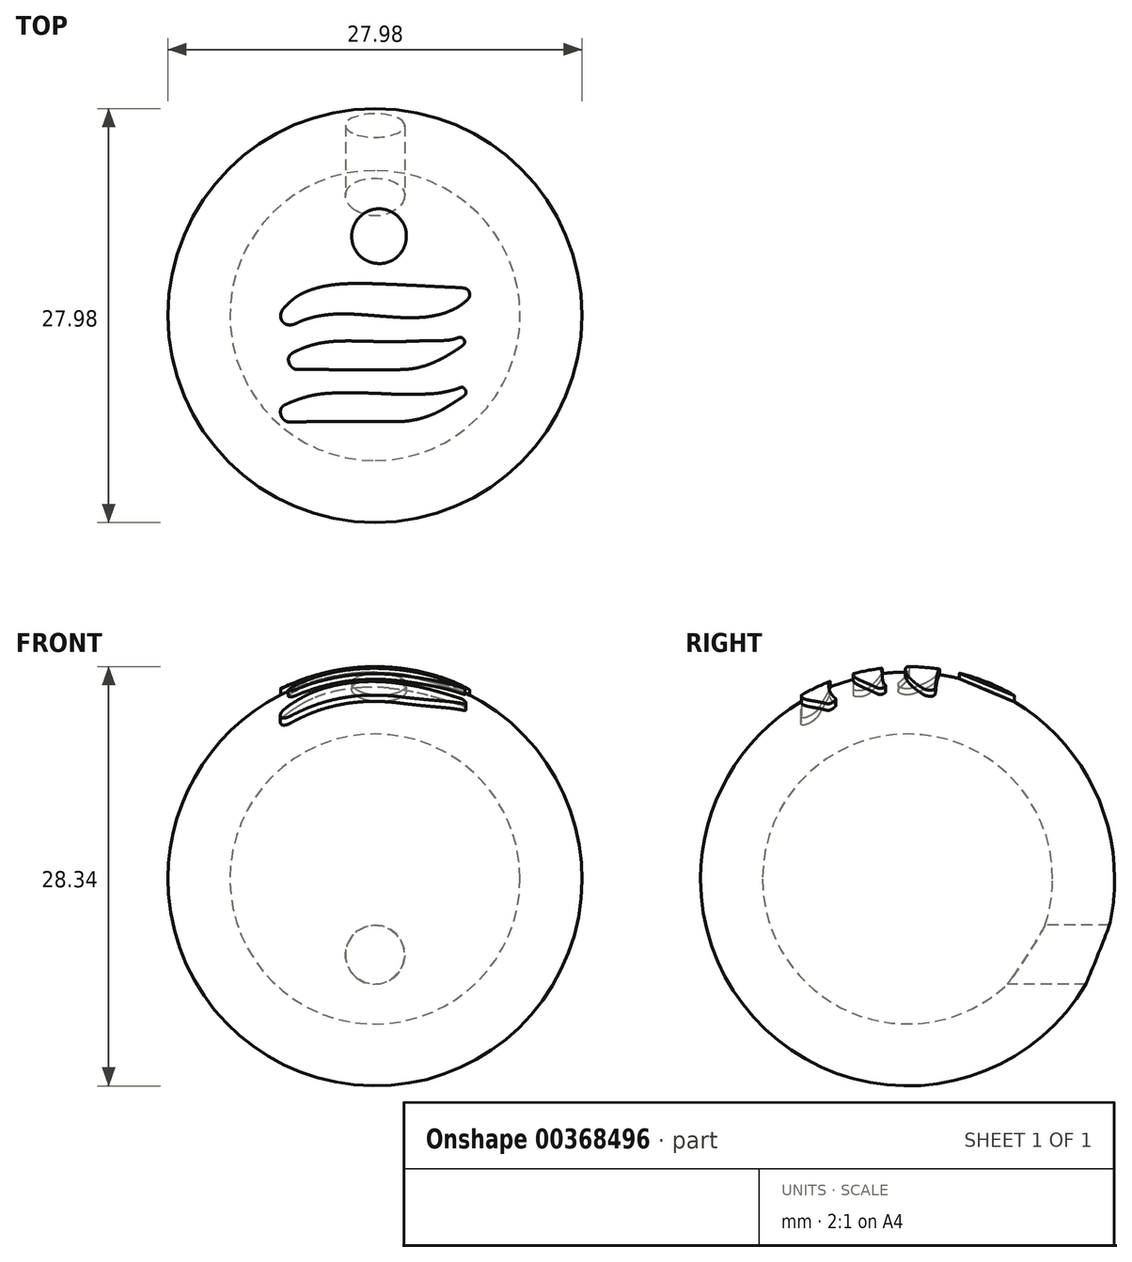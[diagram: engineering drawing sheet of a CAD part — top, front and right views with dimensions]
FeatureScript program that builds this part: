
annotation { "Feature Type Name" : "Feature", "Feature Type Description" : "" }
export const myFeature = defineFeature(function(context is Context, id is Id, definition is map)
    precondition{}
    {
        {
            var Q0;
            Q0=qCreatedBy(makeId("Top.planeOp"),FACE);
            var sketch = newSketch(context, id + "F0", { "sketchPlane" : qUnion([Q0])});
            skLineSegment(sketch, "E0", {"start": v(0, -10) * mm, "end": v(0, 10) * mm});
            skArc(sketch, "E1", {"start": v(0, 10) * mm, "mid": v(-10, 0) * mm, "end": v(0, -10) * mm});
            skSolve(sketch);
        }
        {
            var Q0;
            {var subQ0=sQuery(id+"F0.wireOp",EDGE,"E1");Q0=makeQuery(id+"F0.imprint","IMPRINT",FACE,{"disambiguationData":[TD([[makeQuery(id+"F0.imprint","IMPRINT",EDGE,{"derivedFrom":subQ0}),1.0]])]});}
            var Q1;
            Q1=sQuery(id+"F0.wireOp",EDGE,"E0");
            revolve(context, id + "F1", {"entities" : qUnion([Q0]), "axis" : qUnion([Q1]), "revolveType" : RevolveType.FULL});
        }
        {
            var Q0;
            Q0=makeQuery(id+"F1.opRevolve","SWEPT_BODY",BODY,{"disambiguationData":[OSD([sQuery(id+"F0.wireOp",EDGE,"E0"),sQuery(id+"F0.wireOp",EDGE,"E1")])]});
            var Q1;
            Q1=sQuery(id+"F0.wireOp",VERTEX,"NPe4G0ez-t7S9-9isL-QO5v-uuJu600mHcIT.center");
            var Q2;
            Q2=sQuery(id+"F0.wireOp",VERTEX,"E1.center");
            transform(context, id + "F2", {"entities" : qUnion([Q0]), "transformType" : TransformType.SCALE_UNIFORMLY, "scale" : 33.3, "scalePoint" : qUnion([Q2]), "makeCopy" : false});
        }
        {
            var Q0;
            Q0=qCreatedBy(makeId("Top.planeOp"),FACE);
            var sketch = newSketch(context, id + "F3", { "sketchPlane" : qUnion([Q0])});
            skArc(sketch, "E2", {"start": v(-4.66, 170.28) * mm, "mid": v(-7.58, 169.39) * mm, "end": v(-10.43, 168.3) * mm});
            skArc(sketch, "E3", {"start": v(-10.43, 168.3) * mm, "mid": v(-13.1, 167.06) * mm, "end": v(-15.68, 165.63) * mm});
            skArc(sketch, "E4", {"start": v(-15.68, 165.63) * mm, "mid": v(-18.2, 163.97) * mm, "end": v(-20.58, 162.14) * mm});
            skArc(sketch, "E5", {"start": v(-20.58, 162.14) * mm, "mid": v(-23, 160) * mm, "end": v(-25.3, 157.73) * mm});
            skArc(sketch, "E6", {"start": v(-25.3, 157.73) * mm, "mid": v(-31.47, 149.54) * mm, "end": v(-35.58, 140.15) * mm});
            skArc(sketch, "E7", {"start": v(-35.58, 140.15) * mm, "mid": v(-37.42, 130.07) * mm, "end": v(-36.87, 119.84) * mm});
            skArc(sketch, "E8", {"start": v(-36.87, 119.84) * mm, "mid": v(-33.98, 110.06) * mm, "end": v(-28.9, 101.23) * mm});
            skArc(sketch, "E9", {"start": v(-28.9, 101.23) * mm, "mid": v(-21.93, 93.88) * mm, "end": v(-13.42, 88.39) * mm});
            skArc(sketch, "E10", {"start": v(-13.42, 88.39) * mm, "mid": v(-4.52, 85.1) * mm, "end": v(4.86, 83.64) * mm});
            skArc(sketch, "E11", {"start": v(4.86, 83.64) * mm, "mid": v(14.1, 84.14) * mm, "end": v(23, 86.6) * mm});
            skArc(sketch, "E12", {"start": v(23, 86.6) * mm, "mid": v(31.14, 90.88) * mm, "end": v(38.15, 96.82) * mm});
            skArc(sketch, "E13", {"start": v(38.15, 96.82) * mm, "mid": v(43.87, 104.23) * mm, "end": v(47.95, 112.66) * mm});
            skArc(sketch, "E14", {"start": v(47.95, 112.66) * mm, "mid": v(48.9, 115.67) * mm, "end": v(49.58, 118.75) * mm});
            skArc(sketch, "E15", {"start": v(49.58, 118.75) * mm, "mid": v(50.08, 122.26) * mm, "end": v(50.36, 125.8) * mm});
            skArc(sketch, "E16", {"start": v(50.36, 125.8) * mm, "mid": v(50.43, 129.3) * mm, "end": v(50.27, 132.82) * mm});
            skArc(sketch, "E17", {"start": v(50.27, 132.82) * mm, "mid": v(49.9, 135.86) * mm, "end": v(49.24, 138.85) * mm});
            skArc(sketch, "E18", {"start": v(49.24, 138.85) * mm, "mid": v(46.19, 146.9) * mm, "end": v(41.61, 154.2) * mm});
            skArc(sketch, "E19", {"start": v(41.61, 154.2) * mm, "mid": v(35.64, 160.54) * mm, "end": v(28.58, 165.62) * mm});
            skArc(sketch, "E20", {"start": v(28.58, 165.62) * mm, "mid": v(20.7, 169.25) * mm, "end": v(12.28, 171.3) * mm});
            skArc(sketch, "E21", {"start": v(12.28, 171.3) * mm, "mid": v(3.76, 171.65) * mm, "end": v(-4.66, 170.28) * mm});
            skArc(sketch, "E22", {"start": v(-53.26, 50.77) * mm, "mid": v(-64.06, 49.8) * mm, "end": v(-74.8, 48.33) * mm});
            skArc(sketch, "E23", {"start": v(-74.8, 48.33) * mm, "mid": v(-84.6, 46.48) * mm, "end": v(-94.27, 44.06) * mm});
            skArc(sketch, "E24", {"start": v(-94.27, 44.06) * mm, "mid": v(-102.95, 41.3) * mm, "end": v(-111.44, 38.01) * mm});
            skArc(sketch, "E25", {"start": v(-111.44, 38.01) * mm, "mid": v(-118.91, 34.44) * mm, "end": v(-126.06, 30.25) * mm});
            skArc(sketch, "E26", {"start": v(-126.06, 30.25) * mm, "mid": v(-129.48, 27.88) * mm, "end": v(-132.74, 25.3) * mm});
            skArc(sketch, "E27", {"start": v(-132.74, 25.3) * mm, "mid": v(-136.56, 21.93) * mm, "end": v(-140.26, 18.43) * mm});
            skArc(sketch, "E28", {"start": v(-140.26, 18.43) * mm, "mid": v(-143.63, 15) * mm, "end": v(-146.88, 11.47) * mm});
            skArc(sketch, "E29", {"start": v(-146.88, 11.47) * mm, "mid": v(-148.63, 9.2) * mm, "end": v(-150.04, 6.7) * mm});
            skArc(sketch, "E30", {"start": v(-150.04, 6.7) * mm, "mid": v(-151.12, 3.79) * mm, "end": v(-151.7, 0.72) * mm});
            skArc(sketch, "E31", {"start": v(-151.7, 0.72) * mm, "mid": v(-151.7, -2.28) * mm, "end": v(-151.14, -5.22) * mm});
            skArc(sketch, "E32", {"start": v(-151.14, -5.22) * mm, "mid": v(-150.05, -7.88) * mm, "end": v(-148.44, -10.26) * mm});
            skArc(sketch, "E33", {"start": v(-148.44, -10.26) * mm, "mid": v(-146.42, -12.22) * mm, "end": v(-144.02, -13.69) * mm});
            skArc(sketch, "E34", {"start": v(-144.02, -13.69) * mm, "mid": v(-142.01, -14.5) * mm, "end": v(-139.92, -15.03) * mm});
            skArc(sketch, "E35", {"start": v(-139.92, -15.03) * mm, "mid": v(-137.8, -15.3) * mm, "end": v(-135.66, -15.27) * mm});
            skArc(sketch, "E36", {"start": v(-135.66, -15.27) * mm, "mid": v(-133.36, -14.96) * mm, "end": v(-131.12, -14.38) * mm});
            skArc(sketch, "E37", {"start": v(-131.12, -14.38) * mm, "mid": v(-128.6, -13.46) * mm, "end": v(-126.17, -12.35) * mm});
            skArc(sketch, "E38", {"start": v(-126.17, -12.35) * mm, "mid": v(-117.46, -8.41) * mm, "end": v(-108.44, -5.24) * mm});
            skArc(sketch, "E39", {"start": v(-108.44, -5.24) * mm, "mid": v(-98.18, -2.46) * mm, "end": v(-87.78, -0.33) * mm});
            skArc(sketch, "E40", {"start": v(-87.78, -0.33) * mm, "mid": v(-76.35, 1.3) * mm, "end": v(-64.84, 2.26) * mm});
            skArc(sketch, "E41", {"start": v(-64.84, 2.26) * mm, "mid": v(-52.55, 2.64) * mm, "end": v(-40.26, 2.43) * mm});
            skArc(sketch, "E42", {"start": v(-40.26, 2.43) * mm, "mid": v(-36.4, 2.26) * mm, "end": v(-32.52, 2.05) * mm});
            skArc(sketch, "E43", {"start": v(-32.52, 2.05) * mm, "mid": v(-27.36, 1.73) * mm, "end": v(-22.2, 1.4) * mm});
            skArc(sketch, "E44", {"start": v(-22.2, 1.4) * mm, "mid": v(-16.72, 1.02) * mm, "end": v(-11.24, 0.63) * mm});
            skArc(sketch, "E45", {"start": v(-11.24, 0.63) * mm, "mid": v(-6.25, 0.24) * mm, "end": v(-1.26, -0.16) * mm});
            skArc(sketch, "E46", {"start": v(-1.26, -0.16) * mm, "mid": v(3.81, -0.58) * mm, "end": v(8.89, -0.98) * mm});
            skArc(sketch, "E47", {"start": v(8.89, -0.98) * mm, "mid": v(14.64, -1.41) * mm, "end": v(20.4, -1.83) * mm});
            skArc(sketch, "E48", {"start": v(20.4, -1.83) * mm, "mid": v(25.93, -2.22) * mm, "end": v(31.47, -2.59) * mm});
            skArc(sketch, "E49", {"start": v(31.47, -2.59) * mm, "mid": v(35.82, -2.86) * mm, "end": v(40.17, -3.11) * mm});
            skArc(sketch, "E50", {"start": v(40.17, -3.11) * mm, "mid": v(56.95, -3.55) * mm, "end": v(73.73, -3.04) * mm});
            skArc(sketch, "E51", {"start": v(73.73, -3.04) * mm, "mid": v(87.98, -1.56) * mm, "end": v(102.05, 1.2) * mm});
            skArc(sketch, "E52", {"start": v(102.05, 1.2) * mm, "mid": v(114.17, 4.83) * mm, "end": v(125.84, 9.71) * mm});
            skArc(sketch, "E53", {"start": v(125.84, 9.71) * mm, "mid": v(136.2, 15.52) * mm, "end": v(145.73, 22.6) * mm});
            skArc(sketch, "E54", {"start": v(145.73, 22.6) * mm, "mid": v(146.55, 23.31) * mm, "end": v(147.35, 24.05) * mm});
            skArc(sketch, "E55", {"start": v(147.35, 24.05) * mm, "mid": v(148.14, 24.82) * mm, "end": v(148.9, 25.62) * mm});
            skArc(sketch, "E56", {"start": v(148.9, 25.62) * mm, "mid": v(149.57, 26.35) * mm, "end": v(150.21, 27.1) * mm});
            skArc(sketch, "E57", {"start": v(150.21, 27.1) * mm, "mid": v(150.6, 27.61) * mm, "end": v(150.94, 28.16) * mm});
            skArc(sketch, "E58", {"start": v(150.94, 28.16) * mm, "mid": v(151.52, 29.44) * mm, "end": v(151.89, 30.8) * mm});
            skArc(sketch, "E59", {"start": v(151.89, 30.8) * mm, "mid": v(152.1, 32.43) * mm, "end": v(152.15, 34.07) * mm});
            skArc(sketch, "E60", {"start": v(152.15, 34.07) * mm, "mid": v(152.02, 35.68) * mm, "end": v(151.74, 37.26) * mm});
            skArc(sketch, "E61", {"start": v(151.74, 37.26) * mm, "mid": v(151.32, 38.5) * mm, "end": v(150.68, 39.64) * mm});
            skArc(sketch, "E62", {"start": v(150.68, 39.64) * mm, "mid": v(149.45, 41.07) * mm, "end": v(147.96, 42.23) * mm});
            skArc(sketch, "E63", {"start": v(147.96, 42.23) * mm, "mid": v(146.18, 43.15) * mm, "end": v(144.28, 43.77) * mm});
            skArc(sketch, "E64", {"start": v(144.28, 43.77) * mm, "mid": v(141.31, 44.35) * mm, "end": v(138.3, 44.68) * mm});
            skArc(sketch, "E65", {"start": v(138.3, 44.68) * mm, "mid": v(132.52, 45.03) * mm, "end": v(126.74, 45.3) * mm});
            skArc(sketch, "E66", {"start": v(126.74, 45.3) * mm, "mid": v(122.24, 45.48) * mm, "end": v(117.75, 45.68) * mm});
            skArc(sketch, "E67", {"start": v(117.75, 45.68) * mm, "mid": v(110.73, 46) * mm, "end": v(103.71, 46.34) * mm});
            skArc(sketch, "E68", {"start": v(103.71, 46.34) * mm, "mid": v(95.78, 46.73) * mm, "end": v(87.84, 47.12) * mm});
            skArc(sketch, "E69", {"start": v(87.84, 47.12) * mm, "mid": v(80.04, 47.51) * mm, "end": v(72.24, 47.91) * mm});
            skArc(sketch, "E70", {"start": v(72.24, 47.91) * mm, "mid": v(47.98, 49.13) * mm, "end": v(23.71, 50.25) * mm});
            skArc(sketch, "E71", {"start": v(23.71, 50.25) * mm, "mid": v(7.3, 50.9) * mm, "end": v(-9.1, 51.36) * mm});
            skArc(sketch, "E72", {"start": v(-9.1, 51.36) * mm, "mid": v(-21.25, 51.54) * mm, "end": v(-33.4, 51.52) * mm});
            skArc(sketch, "E73", {"start": v(-33.4, 51.52) * mm, "mid": v(-43.34, 51.29) * mm, "end": v(-53.26, 50.77) * mm});
            skArc(sketch, "E74", {"start": v(132.24, -36.27) * mm, "mid": v(128.84, -37.48) * mm, "end": v(125.36, -38.43) * mm});
            skArc(sketch, "E75", {"start": v(125.36, -38.43) * mm, "mid": v(121.58, -39.19) * mm, "end": v(117.76, -39.7) * mm});
            skArc(sketch, "E76", {"start": v(117.76, -39.7) * mm, "mid": v(112.5, -40.14) * mm, "end": v(107.22, -40.38) * mm});
            skArc(sketch, "E77", {"start": v(107.22, -40.38) * mm, "mid": v(98.48, -40.56) * mm, "end": v(89.74, -40.66) * mm});
            skArc(sketch, "E78", {"start": v(89.74, -40.66) * mm, "mid": v(84.02, -40.72) * mm, "end": v(78.3, -40.8) * mm});
            skArc(sketch, "E79", {"start": v(78.3, -40.8) * mm, "mid": v(72.28, -40.94) * mm, "end": v(66.26, -41.1) * mm});
            skArc(sketch, "E80", {"start": v(66.26, -41.1) * mm, "mid": v(60.8, -41.28) * mm, "end": v(55.33, -41.48) * mm});
            skArc(sketch, "E81", {"start": v(55.33, -41.48) * mm, "mid": v(51.53, -41.66) * mm, "end": v(47.74, -41.9) * mm});
            skArc(sketch, "E82", {"start": v(47.74, -41.9) * mm, "mid": v(43.15, -42.17) * mm, "end": v(38.56, -42.33) * mm});
            skArc(sketch, "E83", {"start": v(38.56, -42.33) * mm, "mid": v(33.12, -42.42) * mm, "end": v(27.68, -42.43) * mm});
            skArc(sketch, "E84", {"start": v(27.68, -42.43) * mm, "mid": v(20.74, -42.36) * mm, "end": v(13.8, -42.21) * mm});
            skArc(sketch, "E85", {"start": v(13.8, -42.21) * mm, "mid": v(4.36, -41.94) * mm, "end": v(-5.07, -41.63) * mm});
            skArc(sketch, "E86", {"start": v(-5.07, -41.63) * mm, "mid": v(-26.65, -41.09) * mm, "end": v(-48.23, -40.97) * mm});
            skArc(sketch, "E87", {"start": v(-48.23, -40.97) * mm, "mid": v(-63.07, -41.48) * mm, "end": v(-77.86, -42.86) * mm});
            skArc(sketch, "E88", {"start": v(-77.86, -42.86) * mm, "mid": v(-89.81, -44.81) * mm, "end": v(-101.57, -47.7) * mm});
            skArc(sketch, "E89", {"start": v(-101.57, -47.7) * mm, "mid": v(-113.32, -51.59) * mm, "end": v(-124.74, -56.33) * mm});
            skArc(sketch, "E90", {"start": v(-124.74, -56.33) * mm, "mid": v(-127.9, -57.83) * mm, "end": v(-131.02, -59.43) * mm});
            skArc(sketch, "E91", {"start": v(-131.02, -59.43) * mm, "mid": v(-132.98, -60.6) * mm, "end": v(-134.82, -61.95) * mm});
            skArc(sketch, "E92", {"start": v(-134.82, -61.95) * mm, "mid": v(-136.11, -63.16) * mm, "end": v(-137.22, -64.54) * mm});
            skArc(sketch, "E93", {"start": v(-137.22, -64.54) * mm, "mid": v(-138.12, -66.08) * mm, "end": v(-138.8, -67.72) * mm});
            skArc(sketch, "E94", {"start": v(-138.8, -67.72) * mm, "mid": v(-139.28, -70.2) * mm, "end": v(-139.15, -72.73) * mm});
            skArc(sketch, "E95", {"start": v(-139.15, -72.73) * mm, "mid": v(-138.4, -75.61) * mm, "end": v(-137.23, -78.35) * mm});
            skArc(sketch, "E96", {"start": v(-137.23, -78.35) * mm, "mid": v(-135.62, -80.94) * mm, "end": v(-133.64, -83.26) * mm});
            skArc(sketch, "E97", {"start": v(-133.64, -83.26) * mm, "mid": v(-131.55, -84.96) * mm, "end": v(-129.14, -86.19) * mm});
            skArc(sketch, "E98", {"start": v(-129.14, -86.19) * mm, "mid": v(-128.26, -86.44) * mm, "end": v(-127.36, -86.53) * mm});
            skArc(sketch, "E99", {"start": v(-127.36, -86.53) * mm, "mid": v(-114.43, -86.69) * mm, "end": v(-101.5, -86.84) * mm});
            skArc(sketch, "E100", {"start": v(-101.5, -86.84) * mm, "mid": v(-86.92, -86.99) * mm, "end": v(-72.34, -87.1) * mm});
            skArc(sketch, "E101", {"start": v(-72.34, -87.1) * mm, "mid": v(-55.23, -87.19) * mm, "end": v(-38.12, -87.25) * mm});
            skArc(sketch, "E102", {"start": v(-38.12, -87.25) * mm, "mid": v(-5.06, -87.3) * mm, "end": v(28, -87.3) * mm});
            skArc(sketch, "E103", {"start": v(28, -87.3) * mm, "mid": v(39.54, -87.11) * mm, "end": v(51.07, -86.6) * mm});
            skArc(sketch, "E104", {"start": v(51.07, -86.6) * mm, "mid": v(58.6, -85.87) * mm, "end": v(66.04, -84.57) * mm});
            skArc(sketch, "E105", {"start": v(66.04, -84.57) * mm, "mid": v(74.26, -82.58) * mm, "end": v(82.35, -80.14) * mm});
            skArc(sketch, "E106", {"start": v(82.35, -80.14) * mm, "mid": v(88.6, -77.93) * mm, "end": v(94.73, -75.44) * mm});
            skArc(sketch, "E107", {"start": v(94.73, -75.44) * mm, "mid": v(101.06, -72.56) * mm, "end": v(107.27, -69.46) * mm});
            skArc(sketch, "E108", {"start": v(107.27, -69.46) * mm, "mid": v(114.04, -65.76) * mm, "end": v(120.68, -61.83) * mm});
            skArc(sketch, "E109", {"start": v(120.68, -61.83) * mm, "mid": v(128.26, -57.07) * mm, "end": v(135.74, -52.14) * mm});
            skArc(sketch, "E110", {"start": v(135.74, -52.14) * mm, "mid": v(138.65, -50.07) * mm, "end": v(141.45, -47.85) * mm});
            skArc(sketch, "E111", {"start": v(141.45, -47.85) * mm, "mid": v(142.88, -46.36) * mm, "end": v(143.94, -44.58) * mm});
            skArc(sketch, "E112", {"start": v(143.94, -44.58) * mm, "mid": v(144.31, -43.02) * mm, "end": v(144.1, -41.42) * mm});
            skArc(sketch, "E113", {"start": v(144.1, -41.42) * mm, "mid": v(143.3, -39.51) * mm, "end": v(142.16, -37.78) * mm});
            skArc(sketch, "E114", {"start": v(142.16, -37.78) * mm, "mid": v(141.3, -36.86) * mm, "end": v(140.3, -36.12) * mm});
            skArc(sketch, "E115", {"start": v(140.3, -36.12) * mm, "mid": v(139.22, -35.6) * mm, "end": v(138.05, -35.3) * mm});
            skArc(sketch, "E116", {"start": v(138.05, -35.3) * mm, "mid": v(136.7, -35.2) * mm, "end": v(135.37, -35.35) * mm});
            skArc(sketch, "E117", {"start": v(135.37, -35.35) * mm, "mid": v(133.78, -35.73) * mm, "end": v(132.24, -36.27) * mm});
            skArc(sketch, "E118", {"start": v(135.24, -116.75) * mm, "mid": v(132.5, -117.85) * mm, "end": v(129.68, -118.77) * mm});
            skArc(sketch, "E119", {"start": v(129.68, -118.77) * mm, "mid": v(125.46, -119.96) * mm, "end": v(121.21, -121.05) * mm});
            skArc(sketch, "E120", {"start": v(121.21, -121.05) * mm, "mid": v(116.55, -122.15) * mm, "end": v(111.87, -123.15) * mm});
            skArc(sketch, "E121", {"start": v(111.87, -123.15) * mm, "mid": v(107.55, -123.97) * mm, "end": v(103.2, -124.67) * mm});
            skArc(sketch, "E122", {"start": v(103.2, -124.67) * mm, "mid": v(96.18, -125.52) * mm, "end": v(89.12, -126.04) * mm});
            skArc(sketch, "E123", {"start": v(89.12, -126.04) * mm, "mid": v(78.35, -126.48) * mm, "end": v(67.57, -126.77) * mm});
            skArc(sketch, "E124", {"start": v(67.57, -126.77) * mm, "mid": v(55.76, -126.9) * mm, "end": v(43.96, -126.87) * mm});
            skArc(sketch, "E125", {"start": v(43.96, -126.87) * mm, "mid": v(33.1, -126.66) * mm, "end": v(22.24, -126.23) * mm});
            skArc(sketch, "E126", {"start": v(22.24, -126.23) * mm, "mid": v(0.62, -125.28) * mm, "end": v(-21.01, -124.56) * mm});
            skArc(sketch, "E127", {"start": v(-21.01, -124.56) * mm, "mid": v(-37.49, -124.27) * mm, "end": v(-53.97, -124.36) * mm});
            skArc(sketch, "E128", {"start": v(-53.97, -124.36) * mm, "mid": v(-66.78, -124.76) * mm, "end": v(-79.57, -125.53) * mm});
            skArc(sketch, "E129", {"start": v(-79.57, -125.53) * mm, "mid": v(-89.46, -126.58) * mm, "end": v(-99.26, -128.24) * mm});
            skArc(sketch, "E130", {"start": v(-99.26, -128.24) * mm, "mid": v(-106.51, -129.88) * mm, "end": v(-113.67, -131.89) * mm});
            skArc(sketch, "E131", {"start": v(-113.67, -131.89) * mm, "mid": v(-121.75, -134.52) * mm, "end": v(-129.74, -137.41) * mm});
            skArc(sketch, "E132", {"start": v(-129.74, -137.41) * mm, "mid": v(-137, -140.3) * mm, "end": v(-144.2, -143.36) * mm});
            skArc(sketch, "E133", {"start": v(-144.2, -143.36) * mm, "mid": v(-147.14, -145.1) * mm, "end": v(-149.61, -147.46) * mm});
            skArc(sketch, "E134", {"start": v(-149.61, -147.46) * mm, "mid": v(-150.87, -149.37) * mm, "end": v(-151.68, -151.5) * mm});
            skArc(sketch, "E135", {"start": v(-151.68, -151.5) * mm, "mid": v(-152.1, -153.97) * mm, "end": v(-152.1, -156.48) * mm});
            skArc(sketch, "E136", {"start": v(-152.1, -156.48) * mm, "mid": v(-151.67, -159.11) * mm, "end": v(-150.83, -161.64) * mm});
            skArc(sketch, "E137", {"start": v(-150.83, -161.64) * mm, "mid": v(-149.6, -164.04) * mm, "end": v(-148.03, -166.23) * mm});
            skArc(sketch, "E138", {"start": v(-148.03, -166.23) * mm, "mid": v(-146.16, -168.12) * mm, "end": v(-143.99, -169.67) * mm});
            skArc(sketch, "E139", {"start": v(-143.99, -169.67) * mm, "mid": v(-141.73, -170.72) * mm, "end": v(-139.3, -171.3) * mm});
            skArc(sketch, "E140", {"start": v(-139.3, -171.3) * mm, "mid": v(-135.4, -171.66) * mm, "end": v(-131.46, -171.7) * mm});
            skArc(sketch, "E141", {"start": v(-131.46, -171.7) * mm, "mid": v(-121.5, -171.4) * mm, "end": v(-111.54, -171.03) * mm});
            skArc(sketch, "E142", {"start": v(-111.54, -171.03) * mm, "mid": v(-103.76, -170.76) * mm, "end": v(-95.98, -170.6) * mm});
            skArc(sketch, "E143", {"start": v(-95.98, -170.6) * mm, "mid": v(-85.5, -170.46) * mm, "end": v(-75.03, -170.38) * mm});
            skArc(sketch, "E144", {"start": v(-75.03, -170.38) * mm, "mid": v(-62.49, -170.34) * mm, "end": v(-49.94, -170.37) * mm});
            skArc(sketch, "E145", {"start": v(-49.94, -170.37) * mm, "mid": v(-35.6, -170.45) * mm, "end": v(-21.26, -170.57) * mm});
            skArc(sketch, "E146", {"start": v(-21.26, -170.57) * mm, "mid": v(-4, -170.74) * mm, "end": v(13.28, -170.87) * mm});
            skArc(sketch, "E147", {"start": v(13.28, -170.87) * mm, "mid": v(22.74, -170.9) * mm, "end": v(32.2, -170.83) * mm});
            skArc(sketch, "E148", {"start": v(32.2, -170.83) * mm, "mid": v(38.3, -170.7) * mm, "end": v(44.39, -170.49) * mm});
            skArc(sketch, "E149", {"start": v(44.39, -170.49) * mm, "mid": v(48.72, -170.2) * mm, "end": v(53.04, -169.72) * mm});
            skArc(sketch, "E150", {"start": v(53.04, -169.72) * mm, "mid": v(59.66, -168.72) * mm, "end": v(66.24, -167.45) * mm});
            skArc(sketch, "E151", {"start": v(66.24, -167.45) * mm, "mid": v(72.42, -166) * mm, "end": v(78.53, -164.27) * mm});
            skArc(sketch, "E152", {"start": v(78.53, -164.27) * mm, "mid": v(84.55, -162.26) * mm, "end": v(90.47, -159.99) * mm});
            skArc(sketch, "E153", {"start": v(90.47, -159.99) * mm, "mid": v(96.6, -157.34) * mm, "end": v(102.62, -154.45) * mm});
            skArc(sketch, "E154", {"start": v(102.62, -154.45) * mm, "mid": v(108.05, -151.59) * mm, "end": v(113.38, -148.53) * mm});
            skArc(sketch, "E155", {"start": v(113.38, -148.53) * mm, "mid": v(120.4, -144.25) * mm, "end": v(127.35, -139.87) * mm});
            skArc(sketch, "E156", {"start": v(127.35, -139.87) * mm, "mid": v(134.12, -135.48) * mm, "end": v(140.85, -131.03) * mm});
            skArc(sketch, "E157", {"start": v(140.85, -131.03) * mm, "mid": v(143.06, -129.3) * mm, "end": v(144.99, -127.28) * mm});
            skArc(sketch, "E158", {"start": v(144.99, -127.28) * mm, "mid": v(145.63, -126.28) * mm, "end": v(146.03, -125.15) * mm});
            skArc(sketch, "E159", {"start": v(146.03, -125.15) * mm, "mid": v(146.2, -123.84) * mm, "end": v(146.15, -122.51) * mm});
            skArc(sketch, "E160", {"start": v(146.15, -122.51) * mm, "mid": v(145.87, -121.14) * mm, "end": v(145.37, -119.84) * mm});
            skArc(sketch, "E161", {"start": v(145.37, -119.84) * mm, "mid": v(144.67, -118.65) * mm, "end": v(143.78, -117.6) * mm});
            skArc(sketch, "E162", {"start": v(143.78, -117.6) * mm, "mid": v(142.83, -116.72) * mm, "end": v(141.82, -115.92) * mm});
            skArc(sketch, "E163", {"start": v(141.82, -115.92) * mm, "mid": v(141.06, -115.52) * mm, "end": v(140.23, -115.33) * mm});
            skArc(sketch, "E164", {"start": v(140.23, -115.33) * mm, "mid": v(139.29, -115.33) * mm, "end": v(138.36, -115.54) * mm});
            skArc(sketch, "E165", {"start": v(138.36, -115.54) * mm, "mid": v(136.79, -116.11) * mm, "end": v(135.24, -116.75) * mm});
            skSolve(sketch);
        }
        {
            var Q0;
            Q0 = qSketchRegion(id + "F3", true);
            var Q1;
            Q1=sQuery(id+"F3.wireOp",EDGE,"E25");
            var Q2;
            Q2=sQuery(id+"F3.wireOp",EDGE,"E24");
            extrude(context, id + "F4", {"entities" : qUnion([Q0]), "operationType" : NewBodyOperationType.ADD, "surfaceEntities" : qUnion([Q1, Q2]), "depth" : 350 * mm});
        }
        {
            var Q0;
            Q0=makeQuery(id+"F4.opExtrude","SWEPT_BODY",BODY,{"disambiguationData":[OSD([sQuery(id+"F3.wireOp",EDGE,"E74"),sQuery(id+"F3.wireOp",EDGE,"E75"),sQuery(id+"F3.wireOp",EDGE,"E76"),sQuery(id+"F3.wireOp",EDGE,"E77"),sQuery(id+"F3.wireOp",EDGE,"E78"),sQuery(id+"F3.wireOp",EDGE,"E79"),sQuery(id+"F3.wireOp",EDGE,"E80"),sQuery(id+"F3.wireOp",EDGE,"E81"),sQuery(id+"F3.wireOp",EDGE,"E82"),sQuery(id+"F3.wireOp",EDGE,"E83"),sQuery(id+"F3.wireOp",EDGE,"E84"),sQuery(id+"F3.wireOp",EDGE,"E85"),sQuery(id+"F3.wireOp",EDGE,"E86"),sQuery(id+"F3.wireOp",EDGE,"E87"),sQuery(id+"F3.wireOp",EDGE,"E88"),sQuery(id+"F3.wireOp",EDGE,"E89"),sQuery(id+"F3.wireOp",EDGE,"E90"),sQuery(id+"F3.wireOp",EDGE,"E91"),sQuery(id+"F3.wireOp",EDGE,"E92"),sQuery(id+"F3.wireOp",EDGE,"E93"),sQuery(id+"F3.wireOp",EDGE,"E94"),sQuery(id+"F3.wireOp",EDGE,"E95"),sQuery(id+"F3.wireOp",EDGE,"E96"),sQuery(id+"F3.wireOp",EDGE,"E97"),sQuery(id+"F3.wireOp",EDGE,"E98"),sQuery(id+"F3.wireOp",EDGE,"E99"),sQuery(id+"F3.wireOp",EDGE,"E100"),sQuery(id+"F3.wireOp",EDGE,"E101"),sQuery(id+"F3.wireOp",EDGE,"E102"),sQuery(id+"F3.wireOp",EDGE,"E103"),sQuery(id+"F3.wireOp",EDGE,"E104"),sQuery(id+"F3.wireOp",EDGE,"E105"),sQuery(id+"F3.wireOp",EDGE,"E106"),sQuery(id+"F3.wireOp",EDGE,"E107"),sQuery(id+"F3.wireOp",EDGE,"E108"),sQuery(id+"F3.wireOp",EDGE,"E109"),sQuery(id+"F3.wireOp",EDGE,"E110"),sQuery(id+"F3.wireOp",EDGE,"E111"),sQuery(id+"F3.wireOp",EDGE,"E112"),sQuery(id+"F3.wireOp",EDGE,"E113"),sQuery(id+"F3.wireOp",EDGE,"E114"),sQuery(id+"F3.wireOp",EDGE,"E115"),sQuery(id+"F3.wireOp",EDGE,"E116"),sQuery(id+"F3.wireOp",EDGE,"E117")])]});
            var Q1;
            Q1=makeQuery(id+"F4.opExtrude","SWEPT_BODY",BODY,{"disambiguationData":[OSD([sQuery(id+"F3.wireOp",EDGE,"E118"),sQuery(id+"F3.wireOp",EDGE,"E119"),sQuery(id+"F3.wireOp",EDGE,"E120"),sQuery(id+"F3.wireOp",EDGE,"E121"),sQuery(id+"F3.wireOp",EDGE,"E122"),sQuery(id+"F3.wireOp",EDGE,"E123"),sQuery(id+"F3.wireOp",EDGE,"E124"),sQuery(id+"F3.wireOp",EDGE,"E125"),sQuery(id+"F3.wireOp",EDGE,"E126"),sQuery(id+"F3.wireOp",EDGE,"E127"),sQuery(id+"F3.wireOp",EDGE,"E128"),sQuery(id+"F3.wireOp",EDGE,"E129"),sQuery(id+"F3.wireOp",EDGE,"E130"),sQuery(id+"F3.wireOp",EDGE,"E131"),sQuery(id+"F3.wireOp",EDGE,"E132"),sQuery(id+"F3.wireOp",EDGE,"E133"),sQuery(id+"F3.wireOp",EDGE,"E134"),sQuery(id+"F3.wireOp",EDGE,"E135"),sQuery(id+"F3.wireOp",EDGE,"E136"),sQuery(id+"F3.wireOp",EDGE,"E137"),sQuery(id+"F3.wireOp",EDGE,"E138"),sQuery(id+"F3.wireOp",EDGE,"E139"),sQuery(id+"F3.wireOp",EDGE,"E140"),sQuery(id+"F3.wireOp",EDGE,"E141"),sQuery(id+"F3.wireOp",EDGE,"E142"),sQuery(id+"F3.wireOp",EDGE,"E143"),sQuery(id+"F3.wireOp",EDGE,"E144"),sQuery(id+"F3.wireOp",EDGE,"E145"),sQuery(id+"F3.wireOp",EDGE,"E146"),sQuery(id+"F3.wireOp",EDGE,"E147"),sQuery(id+"F3.wireOp",EDGE,"E148"),sQuery(id+"F3.wireOp",EDGE,"E149"),sQuery(id+"F3.wireOp",EDGE,"E150"),sQuery(id+"F3.wireOp",EDGE,"E151"),sQuery(id+"F3.wireOp",EDGE,"E152"),sQuery(id+"F3.wireOp",EDGE,"E153"),sQuery(id+"F3.wireOp",EDGE,"E154"),sQuery(id+"F3.wireOp",EDGE,"E155"),sQuery(id+"F3.wireOp",EDGE,"E156"),sQuery(id+"F3.wireOp",EDGE,"E157"),sQuery(id+"F3.wireOp",EDGE,"E158"),sQuery(id+"F3.wireOp",EDGE,"E159"),sQuery(id+"F3.wireOp",EDGE,"E160"),sQuery(id+"F3.wireOp",EDGE,"E161"),sQuery(id+"F3.wireOp",EDGE,"E162"),sQuery(id+"F3.wireOp",EDGE,"E163"),sQuery(id+"F3.wireOp",EDGE,"E164"),sQuery(id+"F3.wireOp",EDGE,"E165")])]});
            var Q2;
            Q2=makeQuery(id+"F4.opExtrude","SWEPT_BODY",BODY,{"disambiguationData":[OSD([sQuery(id+"F3.wireOp",EDGE,"E2"),sQuery(id+"F3.wireOp",EDGE,"E3"),sQuery(id+"F3.wireOp",EDGE,"E4"),sQuery(id+"F3.wireOp",EDGE,"E5"),sQuery(id+"F3.wireOp",EDGE,"E6"),sQuery(id+"F3.wireOp",EDGE,"E7"),sQuery(id+"F3.wireOp",EDGE,"E8"),sQuery(id+"F3.wireOp",EDGE,"E9"),sQuery(id+"F3.wireOp",EDGE,"E10"),sQuery(id+"F3.wireOp",EDGE,"E11"),sQuery(id+"F3.wireOp",EDGE,"E12"),sQuery(id+"F3.wireOp",EDGE,"E13"),sQuery(id+"F3.wireOp",EDGE,"E14"),sQuery(id+"F3.wireOp",EDGE,"E15"),sQuery(id+"F3.wireOp",EDGE,"E16"),sQuery(id+"F3.wireOp",EDGE,"E17"),sQuery(id+"F3.wireOp",EDGE,"E18"),sQuery(id+"F3.wireOp",EDGE,"E19"),sQuery(id+"F3.wireOp",EDGE,"E20"),sQuery(id+"F3.wireOp",EDGE,"E21")])]});
            var Q3;
            Q3=makeQuery(id+"F4.opExtrude","SWEPT_BODY",BODY,{"disambiguationData":[OSD([sQuery(id+"F3.wireOp",EDGE,"E22"),sQuery(id+"F3.wireOp",EDGE,"E23"),sQuery(id+"F3.wireOp",EDGE,"E24"),sQuery(id+"F3.wireOp",EDGE,"E25"),sQuery(id+"F3.wireOp",EDGE,"E26"),sQuery(id+"F3.wireOp",EDGE,"E27"),sQuery(id+"F3.wireOp",EDGE,"E28"),sQuery(id+"F3.wireOp",EDGE,"E29"),sQuery(id+"F3.wireOp",EDGE,"E30"),sQuery(id+"F3.wireOp",EDGE,"E31"),sQuery(id+"F3.wireOp",EDGE,"E32"),sQuery(id+"F3.wireOp",EDGE,"E33"),sQuery(id+"F3.wireOp",EDGE,"E34"),sQuery(id+"F3.wireOp",EDGE,"E35"),sQuery(id+"F3.wireOp",EDGE,"E36"),sQuery(id+"F3.wireOp",EDGE,"E37"),sQuery(id+"F3.wireOp",EDGE,"E38"),sQuery(id+"F3.wireOp",EDGE,"E39"),sQuery(id+"F3.wireOp",EDGE,"E40"),sQuery(id+"F3.wireOp",EDGE,"E41"),sQuery(id+"F3.wireOp",EDGE,"E42"),sQuery(id+"F3.wireOp",EDGE,"E43"),sQuery(id+"F3.wireOp",EDGE,"E44"),sQuery(id+"F3.wireOp",EDGE,"E45"),sQuery(id+"F3.wireOp",EDGE,"E46"),sQuery(id+"F3.wireOp",EDGE,"E47"),sQuery(id+"F3.wireOp",EDGE,"E48"),sQuery(id+"F3.wireOp",EDGE,"E49"),sQuery(id+"F3.wireOp",EDGE,"E50"),sQuery(id+"F3.wireOp",EDGE,"E51"),sQuery(id+"F3.wireOp",EDGE,"E52"),sQuery(id+"F3.wireOp",EDGE,"E53"),sQuery(id+"F3.wireOp",EDGE,"E54"),sQuery(id+"F3.wireOp",EDGE,"E55"),sQuery(id+"F3.wireOp",EDGE,"E56"),sQuery(id+"F3.wireOp",EDGE,"E57"),sQuery(id+"F3.wireOp",EDGE,"E58"),sQuery(id+"F3.wireOp",EDGE,"E59"),sQuery(id+"F3.wireOp",EDGE,"E60"),sQuery(id+"F3.wireOp",EDGE,"E61"),sQuery(id+"F3.wireOp",EDGE,"E62"),sQuery(id+"F3.wireOp",EDGE,"E63"),sQuery(id+"F3.wireOp",EDGE,"E64"),sQuery(id+"F3.wireOp",EDGE,"E65"),sQuery(id+"F3.wireOp",EDGE,"E66"),sQuery(id+"F3.wireOp",EDGE,"E67"),sQuery(id+"F3.wireOp",EDGE,"E68"),sQuery(id+"F3.wireOp",EDGE,"E69"),sQuery(id+"F3.wireOp",EDGE,"E70"),sQuery(id+"F3.wireOp",EDGE,"E71"),sQuery(id+"F3.wireOp",EDGE,"E72"),sQuery(id+"F3.wireOp",EDGE,"E73")])]});
            var Q4;
            Q4=makeQuery(id+"F1.opRevolve","SWEPT_BODY",BODY,{"disambiguationData":[OSD([sQuery(id+"F0.wireOp",EDGE,"E0"),sQuery(id+"F0.wireOp",EDGE,"E1")])]});
            var Q5;
            Q5=qCreatedBy(makeId("Origin.pointOp"),VERTEX);
            transform(context, id + "F5", {"entities" : qUnion([Q0, Q1, Q2, Q3, Q4]), "transformType" : TransformType.SCALE_UNIFORMLY, "scale" : 0.03, "scalePoint" : qUnion([Q5]), "makeCopy" : false});
        }
        {
            var Q0;
            Q0=qCreatedBy(makeId("Top.planeOp"),FACE);
            var sketch = newSketch(context, id + "F6", { "sketchPlane" : qUnion([Q0])});
            skLineSegment(sketch, "E166", {"start": v(0, 15) * mm, "end": v(0, -15) * mm});
            skArc(sketch, "E167", {"start": v(0, 15) * mm, "mid": v(-15, 0) * mm, "end": v(0, -15) * mm});
            skArc(sketch, "E168", {"start": v(0, 10.25) * mm, "mid": v(-10.25, 0) * mm, "end": v(0, -10.25) * mm});
            skArc(sketch, "E169", {"start": v(0, 7) * mm, "mid": v(-7, 0) * mm, "end": v(0, -7) * mm});
            skSolve(sketch);
        }
        {
            var Q0;
            {var subQ0=sQuery(id+"F6.wireOp",EDGE,"E167");Q0=makeQuery(id+"F6.imprint","IMPRINT",FACE,{"disambiguationData":[TD([[makeQuery(id+"F6.imprint","IMPRINT",EDGE,{"derivedFrom":subQ0}),1.0]])]});}
            var Q1;
            {var subQ0=sQuery(id+"F6.wireOp",EDGE,"E169");Q1=makeQuery(id+"F6.imprint","IMPRINT",FACE,{"disambiguationData":[TD([[makeQuery(id+"F6.imprint","IMPRINT",EDGE,{"derivedFrom":subQ0}),1.0]])]});}
            var Q2;
            Q2=sQuery(id+"F6.wireOp",EDGE,"E166");
            revolve(context, id + "F7", {"operationType" : NewBodyOperationType.REMOVE, "entities" : qUnion([Q0, Q1]), "axis" : qUnion([Q2]), "revolveType" : RevolveType.FULL});
        }
        {
            var Q0;
            Q0=makeQuery(id+"F1.opRevolve","SWEPT_BODY",BODY,{"disambiguationData":[OSD([sQuery(id+"F0.wireOp",EDGE,"E0"),sQuery(id+"F0.wireOp",EDGE,"E1")])]});
            var Q1;
            Q1=sQuery(id+"F0.wireOp",VERTEX,"E1.center");
            transform(context, id + "F8", {"entities" : qUnion([Q0]), "transformType" : TransformType.SCALE_UNIFORMLY, "scale" : 1.4, "scalePoint" : qUnion([Q1]), "makeCopy" : false});
        }
        {
            var Q0;
            Q0=qCreatedBy(makeId("Front.planeOp"),FACE);
            var sketch = newSketch(context, id + "F9", { "sketchPlane" : qUnion([Q0])});
            skCircle(sketch, "E170", {"center": v(0, -5.12) * mm, "radius": 2 * mm});
            skSolve(sketch);
        }
        {
            var Q0;
            Q0 = qSketchRegion(id + "F9", true);
            extrude(context, id + "F10", {"entities" : qUnion([Q0]), "operationType" : NewBodyOperationType.REMOVE, "oppositeDirection" : true, "depth" : 25 * mm});
        }
    });
